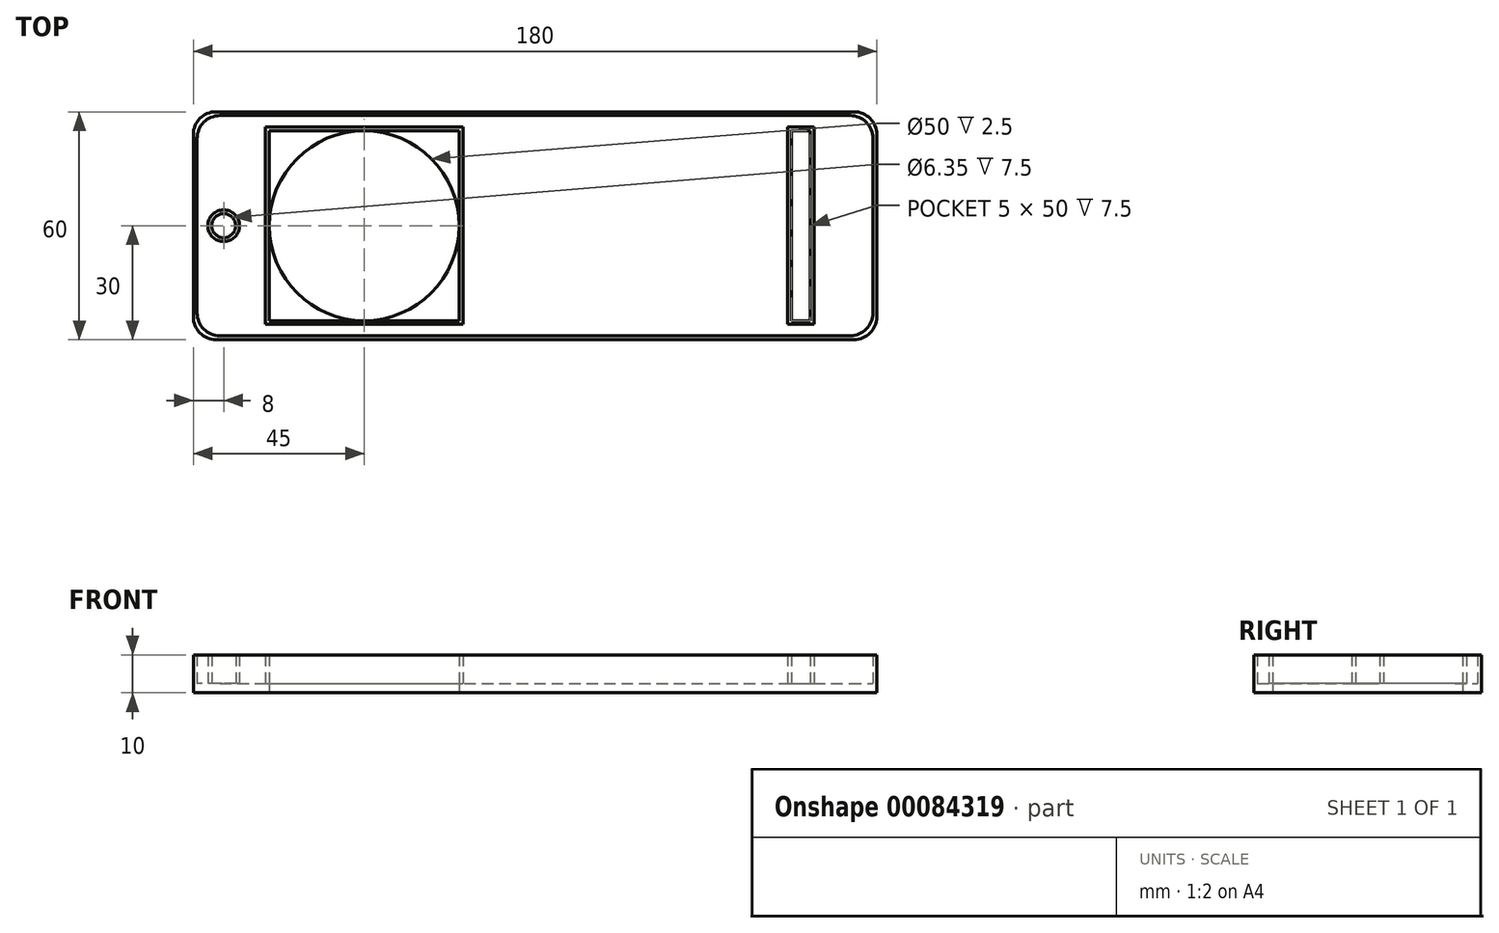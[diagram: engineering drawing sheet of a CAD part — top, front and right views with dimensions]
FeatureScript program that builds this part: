
annotation { "Feature Type Name" : "Feature", "Feature Type Description" : "" }
export const myFeature = defineFeature(function(context is Context, id is Id, definition is map)
    precondition{}
    {
        {
            var Q0;
            Q0=qCreatedBy(makeId("Top.planeOp"),FACE);
            var sketch = newSketch(context, id + "F0", { "sketchPlane" : qUnion([Q0])});
            skLineSegment(sketch, "E0.bottom", {"start": v(84, -30) * mm, "end": v(-84, -30) * mm});
            skLineSegment(sketch, "E0.top", {"start": v(84, 30) * mm, "end": v(-84, 30) * mm});
            skLineSegment(sketch, "E0.left", {"start": v(90, -24) * mm, "end": v(90, 24) * mm});
            skLineSegment(sketch, "E0.right", {"start": v(-90, -24) * mm, "end": v(-90, 24) * mm});
            skPoint(sketch, "E0.middle", {"position": v(0, 0) * mm});
            skPoint(sketch, "E1.startSnap0", {"position": v(-90, 0) * mm});
            skPoint(sketch, "E1.endSnap0", {"position": v(-90, 0) * mm});
            skPoint(sketch, "E2.visualSharp", {"position": v(90, 30) * mm});
            skArc(sketch, "E2.filletArc", {"start": v(90, 24) * mm, "mid": v(88.24, 28.24) * mm, "end": v(84, 30) * mm});
            skPoint(sketch, "E3.visualSharp", {"position": v(90, -30) * mm});
            skArc(sketch, "E3.filletArc", {"start": v(84, -30) * mm, "mid": v(88.24, -28.24) * mm, "end": v(90, -24) * mm});
            skPoint(sketch, "E4.visualSharp", {"position": v(-90, -30) * mm});
            skArc(sketch, "E4.filletArc", {"start": v(-90, -24) * mm, "mid": v(-88.24, -28.24) * mm, "end": v(-84, -30) * mm});
            skPoint(sketch, "E5.visualSharp", {"position": v(-90, 30) * mm});
            skArc(sketch, "E5.filletArc", {"start": v(-84, 30) * mm, "mid": v(-88.24, 28.24) * mm, "end": v(-90, 24) * mm});
            skLineSegment(sketch, "E6", {"start": v(-90, 0) * mm, "end": v(-45, 0) * mm, "construction": true});
            skLineSegment(sketch, "E7.bottom", {"start": v(-20, -25) * mm, "end": v(-70, -25) * mm});
            skLineSegment(sketch, "E7.top", {"start": v(-20, 25) * mm, "end": v(-70, 25) * mm});
            skLineSegment(sketch, "E7.left", {"start": v(-20, -25) * mm, "end": v(-20, 25) * mm});
            skLineSegment(sketch, "E7.right", {"start": v(-70, -25) * mm, "end": v(-70, 25) * mm});
            skPoint(sketch, "E7.middle", {"position": v(-45, 0) * mm});
            skCircle(sketch, "E8", {"center": v(-45, 0) * mm, "radius": 25 * mm});
            skLineSegment(sketch, "E9.bottom", {"start": v(-19, -26) * mm, "end": v(-71, -26) * mm});
            skLineSegment(sketch, "E9.top", {"start": v(-19, 26) * mm, "end": v(-71, 26) * mm});
            skLineSegment(sketch, "E9.left", {"start": v(-19, -26) * mm, "end": v(-19, 26) * mm});
            skLineSegment(sketch, "E9.right", {"start": v(-71, -26) * mm, "end": v(-71, 26) * mm});
            skLineSegment(sketch, "E10", {"start": v(90, 0) * mm, "end": v(70, 0) * mm, "construction": true});
            skPoint(sketch, "E10.endSnap0", {"position": v(90, 0) * mm});
            skLineSegment(sketch, "E11.bottom", {"start": v(72.5, -25) * mm, "end": v(67.5, -25) * mm});
            skLineSegment(sketch, "E11.top", {"start": v(72.5, 25) * mm, "end": v(67.5, 25) * mm});
            skLineSegment(sketch, "E11.left", {"start": v(72.5, -25) * mm, "end": v(72.5, 25) * mm});
            skLineSegment(sketch, "E11.right", {"start": v(67.5, -25) * mm, "end": v(67.5, 25) * mm});
            skPoint(sketch, "E11.middle", {"position": v(70, 0) * mm});
            skLineSegment(sketch, "E12.bottom", {"start": v(73.5, -26) * mm, "end": v(66.5, -26) * mm});
            skLineSegment(sketch, "E12.top", {"start": v(73.5, 26) * mm, "end": v(66.5, 26) * mm});
            skLineSegment(sketch, "E12.left", {"start": v(73.5, -26) * mm, "end": v(73.5, 26) * mm});
            skLineSegment(sketch, "E12.right", {"start": v(66.5, -26) * mm, "end": v(66.5, 26) * mm});
            skLineSegment(sketch, "E13", {"start": v(-90, 0) * mm, "end": v(-82, 0) * mm, "construction": true});
            skCircle(sketch, "E14", {"center": v(-82, 0) * mm, "radius": 3.17 * mm});
            skCircle(sketch, "E15", {"center": v(-82, 0) * mm, "radius": 4.17 * mm});
            skLineSegment(sketch, "E16.bottom", {"start": v(83, -29) * mm, "end": v(-83, -29) * mm});
            skLineSegment(sketch, "E16.top", {"start": v(83, 29) * mm, "end": v(-83, 29) * mm});
            skLineSegment(sketch, "E16.left", {"start": v(89, -23) * mm, "end": v(89, 23) * mm});
            skLineSegment(sketch, "E16.right", {"start": v(-89, -23) * mm, "end": v(-89, 23) * mm});
            skPoint(sketch, "E17.visualSharp", {"position": v(89, 29) * mm});
            skArc(sketch, "E17.filletArc", {"start": v(89, 23) * mm, "mid": v(87.24, 27.24) * mm, "end": v(83, 29) * mm});
            skPoint(sketch, "E18.visualSharp", {"position": v(89, -29) * mm});
            skArc(sketch, "E18.filletArc", {"start": v(83, -29) * mm, "mid": v(87.24, -27.24) * mm, "end": v(89, -23) * mm});
            skPoint(sketch, "E19.visualSharp", {"position": v(-89, -29) * mm});
            skArc(sketch, "E19.filletArc", {"start": v(-89, -23) * mm, "mid": v(-87.24, -27.24) * mm, "end": v(-83, -29) * mm});
            skPoint(sketch, "E20.visualSharp", {"position": v(-89, 29) * mm});
            skArc(sketch, "E20.filletArc", {"start": v(-83, 29) * mm, "mid": v(-87.24, 27.24) * mm, "end": v(-89, 23) * mm});
            skSolve(sketch);
        }
        {
            var Q0;
            Q0=makeQuery(id+"F0.imprint","IMPRINT",FACE,{"disambiguationData":[TD([[makeQuery(id+"F0.imprint","IMPRINT",EDGE,{"derivedFrom":sQuery(id+"F0.wireOp",EDGE,"E0.bottom")}),-1.0]])]});
            var Q1;
            Q1=makeQuery(id+"F0.imprint","IMPRINT",FACE,{"disambiguationData":[TD([[makeQuery(id+"F0.imprint","IMPRINT",EDGE,{"derivedFrom":sQuery(id+"F0.wireOp",EDGE,"E9.bottom")}),-1.0]])]});
            var Q2;
            {var subQ0=sQuery(id+"F0.wireOp",EDGE,"E7.left");var subQ1=sQuery(id+"F0.wireOp",EDGE,"E7.bottom");var subQ2=makeQuery(id+"F0.imprint","INTERSECT",VERTEX,{"derivedFrom":[subQ1,subQ0]});Q2=makeQuery(id+"F0.imprint","IMPRINT",FACE,{"disambiguationData":[TD([[makeQuery(id+"F0.imprint","IMPRINT",EDGE,{"disambiguationData":[TD([[subQ2,-1.0]])],"derivedFrom":subQ1}),-1.0]])]});}
            var Q3;
            {var subQ0=sQuery(id+"F0.wireOp",EDGE,"E7.left");var subQ1=sQuery(id+"F0.wireOp",EDGE,"E7.top");var subQ2=makeQuery(id+"F0.imprint","INTERSECT",VERTEX,{"derivedFrom":[subQ1,subQ0]});Q3=makeQuery(id+"F0.imprint","IMPRINT",FACE,{"disambiguationData":[TD([[makeQuery(id+"F0.imprint","IMPRINT",EDGE,{"disambiguationData":[TD([[subQ2,-1.0]])],"derivedFrom":subQ1}),1.0]])]});}
            var Q4;
            {var subQ0=sQuery(id+"F0.wireOp",EDGE,"E7.right");var subQ1=sQuery(id+"F0.wireOp",EDGE,"E7.top");var subQ2=makeQuery(id+"F0.imprint","INTERSECT",VERTEX,{"derivedFrom":[subQ1,subQ0]});Q4=makeQuery(id+"F0.imprint","IMPRINT",FACE,{"disambiguationData":[TD([[makeQuery(id+"F0.imprint","IMPRINT",EDGE,{"disambiguationData":[TD([[subQ2,1.0]])],"derivedFrom":subQ1}),1.0]])]});}
            var Q5;
            {var subQ0=sQuery(id+"F0.wireOp",EDGE,"E7.right");var subQ1=sQuery(id+"F0.wireOp",EDGE,"E7.bottom");var subQ2=makeQuery(id+"F0.imprint","INTERSECT",VERTEX,{"derivedFrom":[subQ1,subQ0]});Q5=makeQuery(id+"F0.imprint","IMPRINT",FACE,{"disambiguationData":[TD([[makeQuery(id+"F0.imprint","IMPRINT",EDGE,{"disambiguationData":[TD([[subQ2,1.0]])],"derivedFrom":subQ1}),-1.0]])]});}
            var Q6;
            Q6=makeQuery(id+"F0.imprint","IMPRINT",FACE,{"disambiguationData":[TD([[makeQuery(id+"F0.imprint","IMPRINT",EDGE,{"derivedFrom":sQuery(id+"F0.wireOp",EDGE,"E11.bottom")}),1.0]])]});
            var Q7;
            Q7=makeQuery(id+"F0.imprint","IMPRINT",FACE,{"disambiguationData":[TD([[makeQuery(id+"F0.imprint","IMPRINT",EDGE,{"derivedFrom":sQuery(id+"F0.wireOp",EDGE,"E11.bottom")}),-1.0]])]});
            var Q8;
            Q8=makeQuery(id+"F0.imprint","IMPRINT",FACE,{"disambiguationData":[TD([[makeQuery(id+"F0.imprint","IMPRINT",EDGE,{"derivedFrom":sQuery(id+"F0.wireOp",EDGE,"E14")}),1.0]])]});
            var Q9;
            Q9=makeQuery(id+"F0.imprint","IMPRINT",FACE,{"disambiguationData":[TD([[makeQuery(id+"F0.imprint","IMPRINT",EDGE,{"derivedFrom":sQuery(id+"F0.wireOp",EDGE,"E14")}),-1.0]])]});
            var Q10;
            Q10=makeQuery(id+"F0.imprint","IMPRINT",FACE,{"disambiguationData":[TD([[makeQuery(id+"F0.imprint","IMPRINT",EDGE,{"derivedFrom":sQuery(id+"F0.wireOp",EDGE,"E9.bottom")}),1.0]])]});
            extrude(context, id + "F1", {"entities" : qUnion([Q0, Q1, Q2, Q3, Q4, Q5, Q6, Q7, Q8, Q9, Q10]), "depth" : 2.5 * mm});
        }
        {
            var Q0;
            Q0=makeQuery(id+"F0.imprint","IMPRINT",FACE,{"disambiguationData":[TD([[makeQuery(id+"F0.imprint","IMPRINT",EDGE,{"derivedFrom":sQuery(id+"F0.wireOp",EDGE,"E9.bottom")}),-1.0]])]});
            var Q1;
            Q1=makeQuery(id+"F0.imprint","IMPRINT",FACE,{"disambiguationData":[TD([[makeQuery(id+"F0.imprint","IMPRINT",EDGE,{"derivedFrom":sQuery(id+"F0.wireOp",EDGE,"E11.bottom")}),1.0]])]});
            extrude(context, id + "F2", {"entities" : qUnion([Q0, Q1]), "operationType" : NewBodyOperationType.ADD, "depth" : 10 * mm});
        }
        {
            var Q0;
            Q0=makeQuery(id+"F0.imprint","IMPRINT",FACE,{"disambiguationData":[TD([[makeQuery(id+"F0.imprint","IMPRINT",EDGE,{"derivedFrom":sQuery(id+"F0.wireOp",EDGE,"E14")}),-1.0]])]});
            extrude(context, id + "F3", {"entities" : qUnion([Q0]), "operationType" : NewBodyOperationType.ADD, "depth" : 10 * mm});
        }
        {
            var Q0;
            Q0=makeQuery(id+"F0.imprint","IMPRINT",FACE,{"disambiguationData":[TD([[makeQuery(id+"F0.imprint","IMPRINT",EDGE,{"derivedFrom":sQuery(id+"F0.wireOp",EDGE,"E0.bottom")}),-1.0]])]});
            extrude(context, id + "F4", {"entities" : qUnion([Q0]), "operationType" : NewBodyOperationType.ADD, "depth" : 10 * mm});
        }
    });
